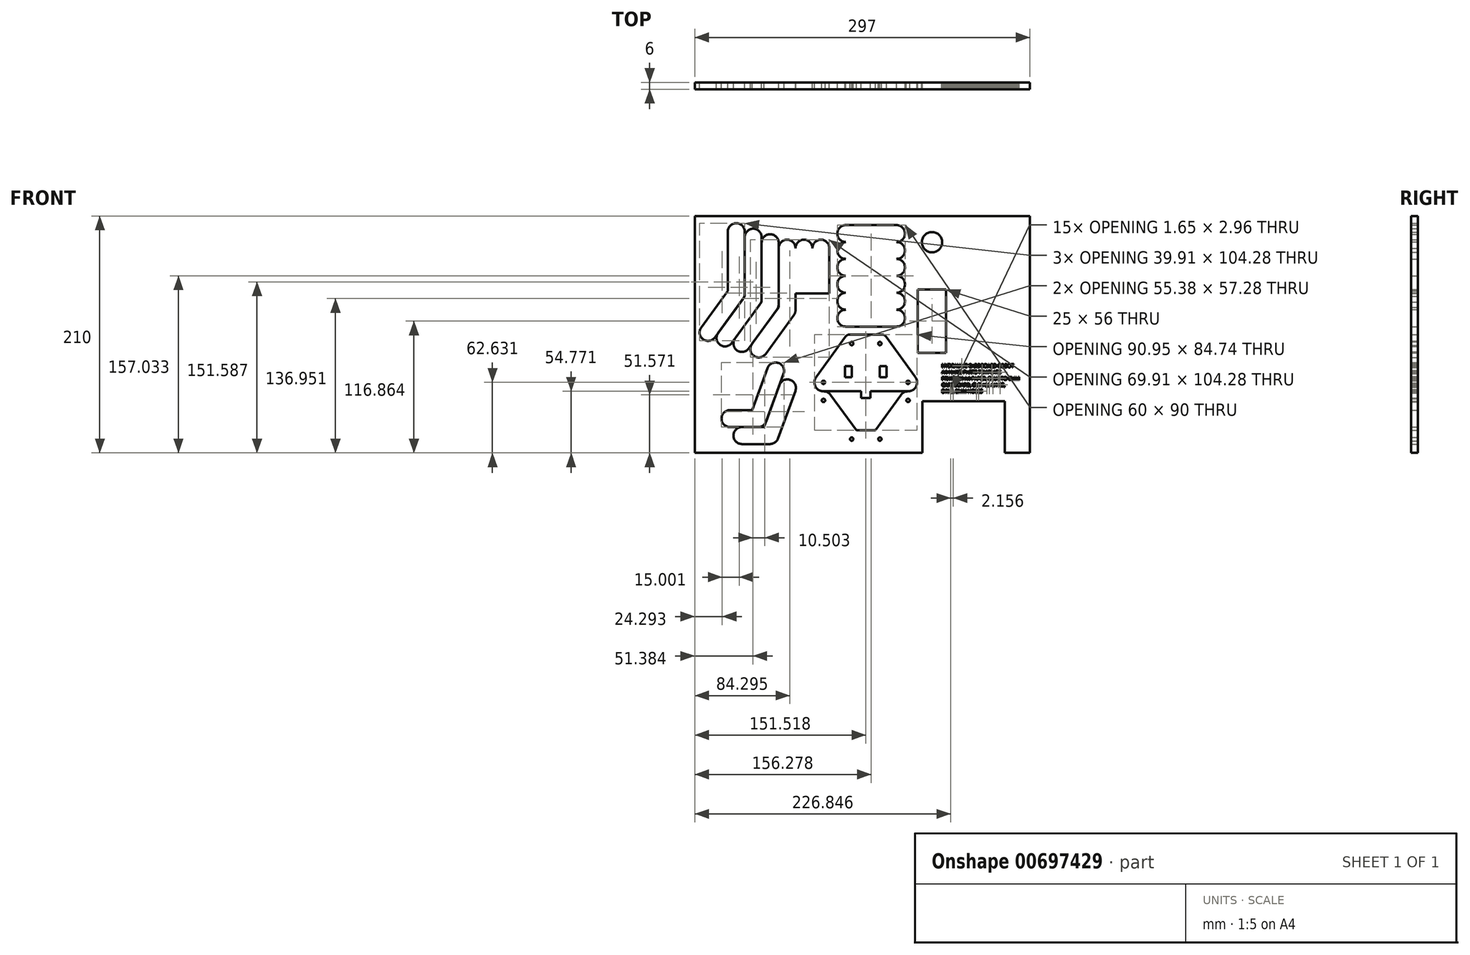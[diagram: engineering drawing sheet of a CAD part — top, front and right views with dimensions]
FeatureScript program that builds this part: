
annotation { "Feature Type Name" : "Feature", "Feature Type Description" : "" }
export const myFeature = defineFeature(function(context is Context, id is Id, definition is map)
    precondition{}
    {
        {
            var Q0;
            Q0=qCreatedBy(makeId("Front.planeOp"),FACE);
            var sketch = newSketch(context, id + "F0", { "sketchPlane" : qUnion([Q0])});
            skLineSegment(sketch, "E0.bottom", {"start": v(148.5, 105) * mm, "end": v(-148.5, 105) * mm});
            skLineSegment(sketch, "E0.top", {"start": v(148.5, -105) * mm, "end": v(-148.5, -105) * mm});
            skLineSegment(sketch, "E0.left", {"start": v(148.5, 105) * mm, "end": v(148.5, -105) * mm});
            skLineSegment(sketch, "E0.right", {"start": v(-148.5, 105) * mm, "end": v(-148.5, -105) * mm});
            skPoint(sketch, "E0.middle", {"position": v(0, 0) * mm});
            skLineSegment(sketch, "E1", {"start": v(-282.28, 34.37) * mm, "end": v(-269.78, 34.37) * mm, "construction": true});
            skLineSegment(sketch, "E2", {"start": v(-269.78, 34.37) * mm, "end": v(-269.78, 0) * mm, "construction": true});
            skLineSegment(sketch, "E3", {"start": v(-269.78, 0) * mm, "end": v(-307.28, 0) * mm, "construction": true});
            skLineSegment(sketch, "E4", {"start": v(-307.28, 0) * mm, "end": v(-282.28, 34.37) * mm, "construction": true});
            skLineSegment(sketch, "E5", {"start": v(-282.28, 34.37) * mm, "end": v(-297.67, 76.66) * mm, "construction": true});
            skLineSegment(sketch, "E6", {"start": v(-297.67, 76.66) * mm, "end": v(-322.67, 42.29) * mm, "construction": true});
            skLineSegment(sketch, "E7", {"start": v(-322.67, 42.29) * mm, "end": v(-307.28, 0) * mm, "construction": true});
            skLineSegment(sketch, "E8", {"start": v(-297.67, 76.66) * mm, "end": v(-297.67, 131.66) * mm, "construction": true});
            skLineSegment(sketch, "E9.MirrorCS", {"start": v(-216.89, 42.29) * mm, "end": v(-232.28, 0) * mm, "construction": true});
            skLineSegment(sketch, "E10.MirrorCS", {"start": v(-257.28, 34.37) * mm, "end": v(-241.89, 76.66) * mm, "construction": true});
            skArc(sketch, "E11.0.startCap", {"start": v(-290.17, 76.66) * mm, "mid": v(-297.67, 69.16) * mm, "end": v(-305.17, 76.66) * mm, "construction": true});
            skArc(sketch, "E11.0.endCap", {"start": v(-305.17, 131.66) * mm, "mid": v(-297.67, 139.16) * mm, "end": v(-290.17, 131.66) * mm, "construction": true});
            skLineSegment(sketch, "E11.0.left", {"start": v(-305.17, 76.66) * mm, "end": v(-305.17, 131.66) * mm, "construction": true});
            skLineSegment(sketch, "E11.0.right", {"start": v(-290.17, 76.66) * mm, "end": v(-290.17, 131.66) * mm, "construction": true});
            skArc(sketch, "E11.1.startCap", {"start": v(-303.74, 81.07) * mm, "mid": v(-293.26, 82.72) * mm, "end": v(-291.6, 72.24) * mm, "construction": true});
            skArc(sketch, "E11.1.endCap", {"start": v(-316.6, 37.87) * mm, "mid": v(-327.08, 36.22) * mm, "end": v(-328.74, 46.7) * mm, "construction": true});
            skLineSegment(sketch, "E11.1.left", {"start": v(-291.6, 72.24) * mm, "end": v(-316.6, 37.87) * mm, "construction": true});
            skLineSegment(sketch, "E11.1.right", {"start": v(-303.74, 81.07) * mm, "end": v(-328.74, 46.7) * mm, "construction": true});
            skArc(sketch, "E12.0.startCap", {"start": v(-250.23, 31.8) * mm, "mid": v(-259.85, 27.32) * mm, "end": v(-264.33, 36.93) * mm, "construction": true});
            skArc(sketch, "E12.0.endCap", {"start": v(-248.94, 79.22) * mm, "mid": v(-239.32, 83.7) * mm, "end": v(-234.84, 74.1) * mm, "construction": true});
            skLineSegment(sketch, "E12.0.left", {"start": v(-264.33, 36.93) * mm, "end": v(-248.94, 79.22) * mm, "construction": true});
            skLineSegment(sketch, "E12.0.right", {"start": v(-250.23, 31.8) * mm, "end": v(-234.84, 74.1) * mm, "construction": true});
            skLineSegment(sketch, "E13", {"start": v(-232.28, 0) * mm, "end": v(-257.28, 0) * mm, "construction": true});
            skArc(sketch, "E14.0.startCap", {"start": v(-232.28, 7.5) * mm, "mid": v(-224.78, 0) * mm, "end": v(-232.28, -7.5) * mm, "construction": true});
            skArc(sketch, "E14.0.endCap", {"start": v(-257.28, -7.5) * mm, "mid": v(-264.78, 0) * mm, "end": v(-257.28, 7.5) * mm, "construction": true});
            skLineSegment(sketch, "E14.0.left", {"start": v(-232.28, -7.5) * mm, "end": v(-257.28, -7.5) * mm, "construction": true});
            skLineSegment(sketch, "E14.0.right", {"start": v(-232.28, 7.5) * mm, "end": v(-257.28, 7.5) * mm, "construction": true});
            skArc(sketch, "E14.1.startCap", {"start": v(-223.94, 44.85) * mm, "mid": v(-214.32, 49.33) * mm, "end": v(-209.84, 39.72) * mm, "construction": true});
            skArc(sketch, "E14.1.endCap", {"start": v(-225.23, -2.57) * mm, "mid": v(-234.85, -7.05) * mm, "end": v(-239.33, 2.57) * mm, "construction": true});
            skLineSegment(sketch, "E14.1.left", {"start": v(-209.84, 39.72) * mm, "end": v(-225.23, -2.57) * mm, "construction": true});
            skLineSegment(sketch, "E14.1.right", {"start": v(-223.94, 44.85) * mm, "end": v(-239.33, 2.57) * mm, "construction": true});
            skLineSegment(sketch, "E15", {"start": v(-111.75, 36.23) * mm, "end": v(-111.75, 91.23) * mm, "construction": true});
            skLineSegment(sketch, "E16", {"start": v(-111.75, 36.23) * mm, "end": v(-136.75, 1.86) * mm, "construction": true});
            skArc(sketch, "E17.0.startCap", {"start": v(-104.25, 36.23) * mm, "mid": v(-104.62, 33.9) * mm, "end": v(-105.69, 31.81) * mm});
            skArc(sketch, "E17.0.endCap", {"start": v(-119.25, 91.23) * mm, "mid": v(-111.75, 98.73) * mm, "end": v(-104.25, 91.23) * mm});
            skLineSegment(sketch, "E17.0.left", {"start": v(-119.25, 38.66) * mm, "end": v(-119.25, 91.23) * mm});
            skLineSegment(sketch, "E17.0.right", {"start": v(-104.25, 36.23) * mm, "end": v(-104.25, 91.23) * mm});
            skArc(sketch, "E17.1.startCap", {"start": v(-104.25, 36.23) * mm, "mid": v(-104.62, 33.9) * mm, "end": v(-105.69, 31.81) * mm});
            skArc(sketch, "E17.1.endCap", {"start": v(-130.69, -2.56) * mm, "mid": v(-141.16, -4.2) * mm, "end": v(-142.82, 6.27) * mm});
            skLineSegment(sketch, "E17.1.left", {"start": v(-105.69, 31.81) * mm, "end": v(-130.69, -2.56) * mm});
            skLineSegment(sketch, "E17.1.right", {"start": v(-119.25, 38.66) * mm, "end": v(-142.82, 6.27) * mm});
            skCircle(sketch, "E18", {"center": v(-111.75, 91.23) * mm, "radius": 1.5 * mm});
            skCircle(sketch, "E19", {"center": v(-111.75, 36.23) * mm, "radius": 1.5 * mm});
            skCircle(sketch, "E20", {"center": v(-136.75, 1.86) * mm, "radius": 1.5 * mm});
            skLineSegment(sketch, "E21", {"start": v(-14.72, 89.53) * mm, "end": v(30.28, 89.53) * mm, "construction": true});
            skArc(sketch, "E22.0.startCap", {"start": v(-14.72, 82.03) * mm, "mid": v(-22.22, 89.53) * mm, "end": v(-14.72, 97.03) * mm});
            skArc(sketch, "E22.0.endCap", {"start": v(30.28, 97.03) * mm, "mid": v(37.78, 89.53) * mm, "end": v(30.28, 82.03) * mm});
            skLineSegment(sketch, "E22.0.left", {"start": v(-14.72, 97.03) * mm, "end": v(30.28, 97.03) * mm});
            skLineSegment(sketch, "E22.0.right", {"start": v(-14.72, 82.03) * mm, "end": v(30.28, 82.03) * mm});
            skCircle(sketch, "E23", {"center": v(-14.72, 89.53) * mm, "radius": 1.5 * mm});
            skCircle(sketch, "E24", {"center": v(30.28, 89.53) * mm, "radius": 1.5 * mm});
            skCircle(sketch, "E25.0.1.1", {"center": v(30.28, 74.53) * mm, "radius": 1.5 * mm});
            skCircle(sketch, "E25.0.1.2", {"center": v(-14.72, 74.53) * mm, "radius": 1.5 * mm});
            skArc(sketch, "E25.0.1.3", {"start": v(30.28, 82.03) * mm, "mid": v(37.78, 74.53) * mm, "end": v(30.28, 67.03) * mm});
            skArc(sketch, "E25.0.1.4", {"start": v(-14.72, 67.03) * mm, "mid": v(-22.22, 74.53) * mm, "end": v(-14.72, 82.03) * mm});
            skLineSegment(sketch, "E25.0.1.5", {"start": v(-14.72, 67.03) * mm, "end": v(30.28, 67.03) * mm});
            skLineSegment(sketch, "E25.0.1.6", {"start": v(-14.72, 74.53) * mm, "end": v(30.28, 74.53) * mm, "construction": true});
            skLineSegment(sketch, "E25.0.2.0", {"start": v(-14.72, 67.03) * mm, "end": v(30.28, 67.03) * mm});
            skCircle(sketch, "E25.0.2.1", {"center": v(30.28, 59.53) * mm, "radius": 1.5 * mm});
            skCircle(sketch, "E25.0.2.2", {"center": v(-14.72, 59.53) * mm, "radius": 1.5 * mm});
            skArc(sketch, "E25.0.2.3", {"start": v(30.28, 67.03) * mm, "mid": v(37.78, 59.53) * mm, "end": v(30.28, 52.03) * mm});
            skArc(sketch, "E25.0.2.4", {"start": v(-14.72, 52.03) * mm, "mid": v(-22.22, 59.53) * mm, "end": v(-14.72, 67.03) * mm});
            skLineSegment(sketch, "E25.0.2.5", {"start": v(-14.72, 52.03) * mm, "end": v(30.28, 52.03) * mm});
            skLineSegment(sketch, "E25.0.2.6", {"start": v(-14.72, 59.53) * mm, "end": v(30.28, 59.53) * mm, "construction": true});
            skLineSegment(sketch, "E25.0.3.0", {"start": v(-14.72, 52.03) * mm, "end": v(30.28, 52.03) * mm});
            skCircle(sketch, "E25.0.3.1", {"center": v(30.28, 44.53) * mm, "radius": 1.5 * mm});
            skCircle(sketch, "E25.0.3.2", {"center": v(-14.72, 44.53) * mm, "radius": 1.5 * mm});
            skArc(sketch, "E25.0.3.3", {"start": v(30.28, 52.03) * mm, "mid": v(37.78, 44.53) * mm, "end": v(30.28, 37.03) * mm});
            skArc(sketch, "E25.0.3.4", {"start": v(-14.72, 37.03) * mm, "mid": v(-22.22, 44.53) * mm, "end": v(-14.72, 52.03) * mm});
            skLineSegment(sketch, "E25.0.3.5", {"start": v(-14.72, 37.03) * mm, "end": v(30.28, 37.03) * mm});
            skLineSegment(sketch, "E25.0.3.6", {"start": v(-14.72, 44.53) * mm, "end": v(30.28, 44.53) * mm, "construction": true});
            skLineSegment(sketch, "E25.0.4.0", {"start": v(-14.72, 37.03) * mm, "end": v(30.28, 37.03) * mm});
            skCircle(sketch, "E25.0.4.1", {"center": v(30.28, 29.53) * mm, "radius": 1.5 * mm});
            skCircle(sketch, "E25.0.4.2", {"center": v(-14.72, 29.53) * mm, "radius": 1.5 * mm});
            skArc(sketch, "E25.0.4.3", {"start": v(30.28, 37.03) * mm, "mid": v(37.78, 29.53) * mm, "end": v(30.28, 22.03) * mm});
            skArc(sketch, "E25.0.4.4", {"start": v(-14.72, 22.03) * mm, "mid": v(-22.22, 29.53) * mm, "end": v(-14.72, 37.03) * mm});
            skLineSegment(sketch, "E25.0.4.5", {"start": v(-14.72, 22.03) * mm, "end": v(30.28, 22.03) * mm});
            skLineSegment(sketch, "E25.0.4.6", {"start": v(-14.72, 29.53) * mm, "end": v(30.28, 29.53) * mm, "construction": true});
            skLineSegment(sketch, "E25.0.5.0", {"start": v(-14.72, 22.03) * mm, "end": v(30.28, 22.03) * mm});
            skCircle(sketch, "E25.0.5.1", {"center": v(30.28, 14.53) * mm, "radius": 1.5 * mm});
            skCircle(sketch, "E25.0.5.2", {"center": v(-14.72, 14.53) * mm, "radius": 1.5 * mm});
            skArc(sketch, "E25.0.5.3", {"start": v(30.28, 22.03) * mm, "mid": v(37.78, 14.53) * mm, "end": v(30.28, 7.03) * mm});
            skArc(sketch, "E25.0.5.4", {"start": v(-14.72, 7.03) * mm, "mid": v(-22.22, 14.53) * mm, "end": v(-14.72, 22.03) * mm});
            skLineSegment(sketch, "E25.0.5.5", {"start": v(-14.72, 7.03) * mm, "end": v(30.28, 7.03) * mm});
            skLineSegment(sketch, "E25.0.5.6", {"start": v(-14.72, 14.53) * mm, "end": v(30.28, 14.53) * mm, "construction": true});
            skLineSegment(sketch, "E25.direction1", {"start": v(-14.72, 82.03) * mm, "end": v(10.98, 82.03) * mm, "construction": true});
            skLineSegment(sketch, "E25.direction2", {"start": v(-14.72, 82.03) * mm, "end": v(-14.72, 67.03) * mm, "construction": true});
            skLineSegment(sketch, "E26", {"start": v(-66.41, -47.28) * mm, "end": v(-81.8, -89.57) * mm, "construction": true});
            skLineSegment(sketch, "E27", {"start": v(-81.8, -89.57) * mm, "end": v(-106.8, -89.57) * mm, "construction": true});
            skArc(sketch, "E28.0.startCap", {"start": v(-73.46, -44.72) * mm, "mid": v(-63.85, -40.24) * mm, "end": v(-59.37, -49.85) * mm});
            skArc(sketch, "E28.0.endCap", {"start": v(-74.76, -92.13) * mm, "mid": v(-77.5, -95.71) * mm, "end": v(-81.8, -97.07) * mm});
            skLineSegment(sketch, "E28.0.left", {"start": v(-59.37, -49.85) * mm, "end": v(-74.76, -92.13) * mm});
            skLineSegment(sketch, "E28.0.right", {"start": v(-73.46, -44.72) * mm, "end": v(-87.06, -82.07) * mm});
            skArc(sketch, "E28.1.startCap", {"start": v(-74.76, -92.13) * mm, "mid": v(-77.5, -95.71) * mm, "end": v(-81.8, -97.07) * mm});
            skArc(sketch, "E28.1.endCap", {"start": v(-106.8, -97.07) * mm, "mid": v(-114.3, -89.57) * mm, "end": v(-106.8, -82.07) * mm});
            skLineSegment(sketch, "E28.1.left", {"start": v(-81.8, -97.07) * mm, "end": v(-106.8, -97.07) * mm});
            skLineSegment(sketch, "E28.1.right", {"start": v(-87.06, -82.07) * mm, "end": v(-106.8, -82.07) * mm});
            skCircle(sketch, "E29", {"center": v(-106.8, -89.57) * mm, "radius": 1.5 * mm});
            skCircle(sketch, "E30", {"center": v(-81.8, -89.57) * mm, "radius": 1.5 * mm});
            skCircle(sketch, "E31", {"center": v(-66.41, -47.28) * mm, "radius": 1.5 * mm});
            skArc(sketch, "E32.0.1.0", {"start": v(-83.96, -29.72) * mm, "mid": v(-74.35, -25.24) * mm, "end": v(-69.87, -34.85) * mm});
            skLineSegment(sketch, "E32.0.1.1", {"start": v(-76.92, -32.28) * mm, "end": v(-92.3, -74.57) * mm, "construction": true});
            skLineSegment(sketch, "E32.0.1.2", {"start": v(-97.56, -67.07) * mm, "end": v(-117.3, -67.07) * mm});
            skLineSegment(sketch, "E32.0.1.3", {"start": v(-69.87, -34.85) * mm, "end": v(-85.26, -77.13) * mm});
            skLineSegment(sketch, "E32.0.1.4", {"start": v(-92.3, -82.07) * mm, "end": v(-117.3, -82.07) * mm});
            skArc(sketch, "E32.0.1.5", {"start": v(-85.26, -77.13) * mm, "mid": v(-88, -80.71) * mm, "end": v(-92.3, -82.07) * mm});
            skCircle(sketch, "E32.0.1.6", {"center": v(-117.3, -74.57) * mm, "radius": 1.5 * mm});
            skCircle(sketch, "E32.0.1.7", {"center": v(-76.92, -32.28) * mm, "radius": 1.5 * mm});
            skArc(sketch, "E32.0.1.8", {"start": v(-117.3, -82.07) * mm, "mid": v(-124.8, -74.57) * mm, "end": v(-117.3, -67.07) * mm});
            skLineSegment(sketch, "E32.0.1.9", {"start": v(-92.3, -74.57) * mm, "end": v(-117.3, -74.57) * mm, "construction": true});
            skCircle(sketch, "E32.0.1.10", {"center": v(-92.3, -74.57) * mm, "radius": 1.5 * mm});
            skLineSegment(sketch, "E32.0.1.11", {"start": v(-83.96, -29.72) * mm, "end": v(-97.56, -67.07) * mm});
            skArc(sketch, "E32.0.1.12", {"start": v(-85.26, -77.13) * mm, "mid": v(-88, -80.71) * mm, "end": v(-92.3, -82.07) * mm});
            skLineSegment(sketch, "E32.direction1", {"start": v(-106.8, -97.07) * mm, "end": v(-72.94, -97.07) * mm, "construction": true});
            skLineSegment(sketch, "E32.direction2", {"start": v(-106.8, -97.07) * mm, "end": v(-117.3, -82.07) * mm, "construction": true});
            skLineSegment(sketch, "E33.1.0.0", {"start": v(-104.25, 33.79) * mm, "end": v(-104.25, 86.35) * mm});
            skLineSegment(sketch, "E33.1.0.1", {"start": v(-90.69, 26.94) * mm, "end": v(-115.69, -7.43) * mm});
            skLineSegment(sketch, "E33.1.0.2", {"start": v(-104.25, 33.79) * mm, "end": v(-127.82, 1.39) * mm});
            skCircle(sketch, "E33.1.0.3", {"center": v(-96.75, 31.35) * mm, "radius": 1.5 * mm});
            skArc(sketch, "E33.1.0.4", {"start": v(-89.25, 31.35) * mm, "mid": v(-89.62, 29.03) * mm, "end": v(-90.69, 26.94) * mm});
            skCircle(sketch, "E33.1.0.5", {"center": v(-121.75, -3.02) * mm, "radius": 1.5 * mm});
            skLineSegment(sketch, "E33.1.0.6", {"start": v(-96.75, 31.35) * mm, "end": v(-121.75, -3.02) * mm, "construction": true});
            skCircle(sketch, "E33.1.0.7", {"center": v(-96.75, 86.35) * mm, "radius": 1.5 * mm});
            skArc(sketch, "E33.1.0.8", {"start": v(-115.69, -7.43) * mm, "mid": v(-126.16, -9.09) * mm, "end": v(-127.82, 1.39) * mm});
            skArc(sketch, "E33.1.0.9", {"start": v(-89.25, 31.35) * mm, "mid": v(-89.62, 29.03) * mm, "end": v(-90.69, 26.94) * mm});
            skLineSegment(sketch, "E33.1.0.10", {"start": v(-96.75, 31.35) * mm, "end": v(-96.75, 86.35) * mm, "construction": true});
            skLineSegment(sketch, "E33.1.0.11", {"start": v(-89.25, 31.35) * mm, "end": v(-89.25, 86.35) * mm});
            skArc(sketch, "E33.1.0.12", {"start": v(-104.25, 86.35) * mm, "mid": v(-96.75, 93.85) * mm, "end": v(-89.25, 86.35) * mm});
            skLineSegment(sketch, "E33.2.0.0", {"start": v(-89.25, 28.9) * mm, "end": v(-89.25, 81.47) * mm});
            skLineSegment(sketch, "E33.2.0.1", {"start": v(-75.69, 22.06) * mm, "end": v(-100.69, -12.31) * mm});
            skLineSegment(sketch, "E33.2.0.2", {"start": v(-89.25, 28.9) * mm, "end": v(-112.82, -3.49) * mm});
            skCircle(sketch, "E33.2.0.3", {"center": v(-81.75, 26.47) * mm, "radius": 1.5 * mm});
            skArc(sketch, "E33.2.0.4", {"start": v(-74.25, 26.47) * mm, "mid": v(-74.62, 24.15) * mm, "end": v(-75.69, 22.06) * mm});
            skCircle(sketch, "E33.2.0.5", {"center": v(-106.75, -7.9) * mm, "radius": 1.5 * mm});
            skLineSegment(sketch, "E33.2.0.6", {"start": v(-81.75, 26.47) * mm, "end": v(-106.75, -7.9) * mm, "construction": true});
            skCircle(sketch, "E33.2.0.7", {"center": v(-81.75, 81.47) * mm, "radius": 1.5 * mm});
            skArc(sketch, "E33.2.0.8", {"start": v(-100.69, -12.31) * mm, "mid": v(-111.16, -13.97) * mm, "end": v(-112.82, -3.49) * mm});
            skArc(sketch, "E33.2.0.9", {"start": v(-74.25, 26.47) * mm, "mid": v(-74.62, 24.15) * mm, "end": v(-75.69, 22.06) * mm});
            skLineSegment(sketch, "E33.2.0.10", {"start": v(-81.75, 26.47) * mm, "end": v(-81.75, 81.47) * mm, "construction": true});
            skLineSegment(sketch, "E33.2.0.11", {"start": v(-74.25, 26.47) * mm, "end": v(-74.25, 81.47) * mm});
            skArc(sketch, "E33.2.0.12", {"start": v(-89.25, 81.47) * mm, "mid": v(-81.75, 88.97) * mm, "end": v(-74.25, 81.47) * mm});
            skLineSegment(sketch, "E33.3.0.0", {"start": v(-74.25, 24.03) * mm, "end": v(-74.25, 76.59) * mm});
            skLineSegment(sketch, "E33.3.0.1", {"start": v(-60.69, 17.18) * mm, "end": v(-85.69, -17.2) * mm});
            skLineSegment(sketch, "E33.3.0.2", {"start": v(-74.25, 24.03) * mm, "end": v(-97.82, -8.37) * mm});
            skCircle(sketch, "E33.3.0.3", {"center": v(-66.75, 21.59) * mm, "radius": 1.5 * mm});
            skArc(sketch, "E33.3.0.4", {"start": v(-59.25, 21.59) * mm, "mid": v(-59.62, 19.27) * mm, "end": v(-60.69, 17.18) * mm});
            skCircle(sketch, "E33.3.0.5", {"center": v(-91.75, -12.78) * mm, "radius": 1.5 * mm});
            skLineSegment(sketch, "E33.3.0.6", {"start": v(-66.75, 21.59) * mm, "end": v(-91.75, -12.78) * mm, "construction": true});
            skCircle(sketch, "E33.3.0.7", {"center": v(-66.75, 76.59) * mm, "radius": 1.5 * mm});
            skArc(sketch, "E33.3.0.8", {"start": v(-85.69, -17.2) * mm, "mid": v(-96.16, -18.84) * mm, "end": v(-97.82, -8.37) * mm});
            skArc(sketch, "E33.3.0.9", {"start": v(-59.25, 21.59) * mm, "mid": v(-59.62, 19.27) * mm, "end": v(-60.69, 17.18) * mm});
            skLineSegment(sketch, "E33.3.0.10", {"start": v(-66.75, 21.59) * mm, "end": v(-66.75, 76.59) * mm, "construction": true});
            skLineSegment(sketch, "E33.3.0.11", {"start": v(-59.25, 21.59) * mm, "end": v(-59.25, 76.59) * mm});
            skArc(sketch, "E33.3.0.12", {"start": v(-74.25, 76.59) * mm, "mid": v(-66.75, 84.09) * mm, "end": v(-59.25, 76.59) * mm});
            skLineSegment(sketch, "E33.direction1", {"start": v(-142.82, 6.27) * mm, "end": v(-127.82, 1.39) * mm, "construction": true});
            skLineSegment(sketch, "E34", {"start": v(3.02, -8) * mm, "end": v(-9.48, -8) * mm, "construction": true});
            skLineSegment(sketch, "E35", {"start": v(-9.48, -8) * mm, "end": v(-34.48, -42.37) * mm, "construction": true});
            skLineSegment(sketch, "E36", {"start": v(-34.48, -42.37) * mm, "end": v(3.02, -42.37) * mm, "construction": true});
            skLineSegment(sketch, "E37", {"start": v(3.02, -42.37) * mm, "end": v(3.02, -8) * mm, "construction": true});
            skLineSegment(sketch, "E38.0", {"start": v(3.02, 0) * mm, "end": v(-11, 0) * mm});
            skLineSegment(sketch, "E38.2", {"start": v(-34.48, -50.37) * mm, "end": v(-0.98, -50.37) * mm});
            skLineSegment(sketch, "E38.3", {"start": v(-15.05, -2.06) * mm, "end": v(-40.95, -37.66) * mm});
            skPoint(sketch, "E39.visualSharp", {"position": v(-13.56, 0) * mm});
            skArc(sketch, "E39.filletArc", {"start": v(-11, 0) * mm, "mid": v(-13.28, -0.54) * mm, "end": v(-15.05, -2.06) * mm});
            skPoint(sketch, "E40.visualSharp", {"position": v(-50.2, -50.37) * mm});
            skLineSegment(sketch, "E41", {"start": v(3.02, -8) * mm, "end": v(3.02, 0) * mm, "construction": true});
            skLineSegment(sketch, "E42", {"start": v(3.02, -42.37) * mm, "end": v(3.02, -50.37) * mm, "construction": true});
            skCircle(sketch, "E43", {"center": v(-9.48, -8) * mm, "radius": 1.5 * mm});
            skCircle(sketch, "E44", {"center": v(-34.48, -42.37) * mm, "radius": 1.5 * mm});
            skLineSegment(sketch, "E45.MirrorCS", {"start": v(40.52, -50.37) * mm, "end": v(7.02, -50.37) * mm});
            skArc(sketch, "E46.MirrorCS", {"start": v(17.05, 0) * mm, "mid": v(19.31, -0.54) * mm, "end": v(21.09, -2.06) * mm});
            skLineSegment(sketch, "E47.MirrorCS", {"start": v(40.52, -42.37) * mm, "end": v(3.02, -42.37) * mm, "construction": true});
            skCircle(sketch, "E48.MirrorC", {"center": v(15.52, -8) * mm, "radius": 1.5 * mm});
            skLineSegment(sketch, "E49.MirrorCS", {"start": v(21.09, -2.06) * mm, "end": v(46.99, -37.66) * mm});
            skLineSegment(sketch, "E50.MirrorCS", {"start": v(3.02, -8) * mm, "end": v(15.52, -8) * mm, "construction": true});
            skCircle(sketch, "E51.MirrorC", {"center": v(40.52, -42.37) * mm, "radius": 1.5 * mm});
            skPoint(sketch, "E52.MirrorP", {"position": v(19.6, 0) * mm});
            skLineSegment(sketch, "E53.MirrorCS", {"start": v(15.52, -8) * mm, "end": v(40.52, -42.37) * mm, "construction": true});
            skLineSegment(sketch, "E54.MirrorCS", {"start": v(3.02, 0) * mm, "end": v(17.05, 0) * mm});
            skLineSegment(sketch, "E55.MirrorCS", {"start": v(3.02, -58.37) * mm, "end": v(3.02, -50.37) * mm, "construction": true});
            skLineSegment(sketch, "E56.MirrorCS", {"start": v(3.02, -100.74) * mm, "end": v(17.05, -100.74) * mm});
            skPoint(sketch, "E57.MirrorP", {"position": v(-13.56, -100.74) * mm});
            skLineSegment(sketch, "E58.MirrorCS", {"start": v(3.02, -92.74) * mm, "end": v(15.52, -92.74) * mm, "construction": true});
            skLineSegment(sketch, "E59.MirrorCS", {"start": v(40.52, -58.37) * mm, "end": v(3.02, -58.37) * mm, "construction": true});
            skLineSegment(sketch, "E60.MirrorCS", {"start": v(3.02, -100.74) * mm, "end": v(-11, -100.74) * mm});
            skLineSegment(sketch, "E61.MirrorCS", {"start": v(3.02, -92.74) * mm, "end": v(-9.48, -92.74) * mm, "construction": true});
            skCircle(sketch, "E62.MirrorC", {"center": v(-9.48, -92.74) * mm, "radius": 1.5 * mm});
            skArc(sketch, "E63.MirrorCS", {"start": v(-11, -100.74) * mm, "mid": v(-13.28, -100.2) * mm, "end": v(-15.05, -98.68) * mm});
            skLineSegment(sketch, "E64.MirrorCS", {"start": v(-9.48, -92.74) * mm, "end": v(-34.48, -58.37) * mm, "construction": true});
            skCircle(sketch, "E65.MirrorC", {"center": v(-34.48, -58.37) * mm, "radius": 1.5 * mm});
            skCircle(sketch, "E66.MirrorC", {"center": v(40.52, -58.37) * mm, "radius": 1.5 * mm});
            skCircle(sketch, "E67.MirrorC", {"center": v(15.52, -92.74) * mm, "radius": 1.5 * mm});
            skLineSegment(sketch, "E68.MirrorCS", {"start": v(-15.05, -98.68) * mm, "end": v(-40.95, -63.08) * mm});
            skPoint(sketch, "E69.MirrorP", {"position": v(19.6, -100.74) * mm});
            skLineSegment(sketch, "E70.MirrorCS", {"start": v(-34.48, -58.37) * mm, "end": v(3.02, -58.37) * mm, "construction": true});
            skLineSegment(sketch, "E71.MirrorCS", {"start": v(3.02, -92.74) * mm, "end": v(3.02, -100.74) * mm, "construction": true});
            skLineSegment(sketch, "E72.MirrorCS", {"start": v(15.52, -92.74) * mm, "end": v(40.52, -58.37) * mm, "construction": true});
            skLineSegment(sketch, "E73.MirrorCS", {"start": v(21.09, -98.68) * mm, "end": v(46.99, -63.08) * mm});
            skArc(sketch, "E74.MirrorCS", {"start": v(17.05, -100.74) * mm, "mid": v(19.31, -100.2) * mm, "end": v(21.09, -98.68) * mm});
            skLineSegment(sketch, "E75.MirrorCS", {"start": v(3.02, -58.37) * mm, "end": v(3.02, -92.74) * mm, "construction": true});
            skLineSegment(sketch, "E76.bottom", {"start": v(-15.48, -27.87) * mm, "end": v(-9.48, -27.87) * mm});
            skLineSegment(sketch, "E76.top", {"start": v(-15.48, -37.87) * mm, "end": v(-9.48, -37.87) * mm});
            skLineSegment(sketch, "E76.left", {"start": v(-15.48, -27.87) * mm, "end": v(-15.48, -37.87) * mm});
            skLineSegment(sketch, "E76.right", {"start": v(-9.48, -27.87) * mm, "end": v(-9.48, -37.87) * mm});
            skLineSegment(sketch, "E77.MirrorCS", {"start": v(21.52, -27.87) * mm, "end": v(21.52, -37.87) * mm});
            skLineSegment(sketch, "E78.MirrorCS", {"start": v(21.52, -37.87) * mm, "end": v(15.52, -37.87) * mm});
            skLineSegment(sketch, "E79.MirrorCS", {"start": v(21.52, -27.87) * mm, "end": v(15.52, -27.87) * mm});
            skLineSegment(sketch, "E80.MirrorCS", {"start": v(15.52, -27.87) * mm, "end": v(15.52, -37.87) * mm});
            skLineSegment(sketch, "E81", {"start": v(7.02, -50.37) * mm, "end": v(7.02, -56.37) * mm});
            skLineSegment(sketch, "E82", {"start": v(7.02, -56.37) * mm, "end": v(-0.98, -56.37) * mm});
            skLineSegment(sketch, "E83", {"start": v(-0.98, -56.37) * mm, "end": v(-0.98, -50.37) * mm});
            skPoint(sketch, "E84.orphan", {"position": v(3.02, -50.37) * mm});
            skPoint(sketch, "E85", {"position": v(3.02, -56.37) * mm});
            skLineSegment(sketch, "E86.bottom", {"start": v(49.18, 95.86) * mm, "end": v(74.18, 95.86) * mm});
            skLineSegment(sketch, "E86.top", {"start": v(49.18, 39.86) * mm, "end": v(74.18, 39.86) * mm});
            skLineSegment(sketch, "E86.left", {"start": v(49.18, 95.86) * mm, "end": v(49.18, 39.86) * mm});
            skLineSegment(sketch, "E86.right", {"start": v(74.18, 95.86) * mm, "end": v(74.18, 39.86) * mm});
            skCircle(sketch, "E87", {"center": v(61.68, 81.86) * mm, "radius": 9 * mm});
            skPoint(sketch, "E87.centerSnap0", {"position": v(61.68, 95.86) * mm});
            skLineSegment(sketch, "E88.MirrorCS", {"start": v(49.18, -16.14) * mm, "end": v(74.18, -16.14) * mm});
            skLineSegment(sketch, "E89.MirrorCS", {"start": v(49.18, -16.14) * mm, "end": v(49.18, 39.86) * mm});
            skCircle(sketch, "E90.MirrorC", {"center": v(61.68, -2.14) * mm, "radius": 9 * mm});
            skPoint(sketch, "E91.MirrorP", {"position": v(61.68, -16.14) * mm});
            skLineSegment(sketch, "E92.MirrorCS", {"start": v(74.18, -16.14) * mm, "end": v(74.18, 39.86) * mm});
            skCircle(sketch, "E93", {"center": v(-66.75, 21.59) * mm, "radius": 7.5 * mm, "construction": true});
            skLineSegment(sketch, "E94", {"start": v(-74.25, 36.59) * mm, "end": v(-59.25, 36.59) * mm, "construction": true});
            skLineSegment(sketch, "E95.1.0.0", {"start": v(-51.75, 21.59) * mm, "end": v(-51.75, 76.59) * mm, "construction": true});
            skArc(sketch, "E95.1.0.2", {"start": v(-59.25, 76.59) * mm, "mid": v(-51.75, 84.09) * mm, "end": v(-44.25, 76.59) * mm});
            skLineSegment(sketch, "E95.1.0.3", {"start": v(-44.25, 21.59) * mm, "end": v(-44.25, 27.85) * mm, "construction": true});
            skCircle(sketch, "E95.1.0.4", {"center": v(-51.75, 76.59) * mm, "radius": 1.5 * mm});
            skLineSegment(sketch, "E95.direction1", {"start": v(-74.25, 76.59) * mm, "end": v(-59.25, 76.59) * mm, "construction": true});
            skLineSegment(sketch, "E96", {"start": v(-44.25, 27.85) * mm, "end": v(-44.25, 76.59) * mm});
            skLineSegment(sketch, "E97.0.2.0", {"start": v(-36.75, 21.59) * mm, "end": v(-36.75, 76.59) * mm, "construction": true});
            skArc(sketch, "E97.6.2.0", {"start": v(-44.25, 76.59) * mm, "mid": v(-36.75, 84.09) * mm, "end": v(-29.25, 76.59) * mm});
            skLineSegment(sketch, "E97.10.2.0", {"start": v(-29.25, 21.59) * mm, "end": v(-29.25, 36.59) * mm, "construction": true});
            skCircle(sketch, "E97.13.2.0", {"center": v(-36.75, 76.59) * mm, "radius": 1.5 * mm});
            skLineSegment(sketch, "E98", {"start": v(-29.25, 36.59) * mm, "end": v(-29.25, 76.59) * mm});
            skLineSegment(sketch, "E99", {"start": v(-29.25, 36.59) * mm, "end": v(-59.25, 36.59) * mm});
            skLineSegment(sketch, "E100", {"start": v(-119.25, 38.66) * mm, "end": v(-111.75, 36.23) * mm, "construction": true});
            skLineSegment(sketch, "E101", {"start": v(-119.25, 38.66) * mm, "end": v(-110.67, 50.47) * mm, "construction": true});
            skLineSegment(sketch, "E102", {"start": v(-92.3, -74.57) * mm, "end": v(-97.56, -67.07) * mm, "construction": true});
            skLineSegment(sketch, "E103", {"start": v(-92.3, -74.57) * mm, "end": v(-83.97, -74.57) * mm, "construction": true});
            skCircle(sketch, "E104", {"center": v(-260.8, -49.84) * mm, "radius": 25 * mm, "construction": true});
            skLineSegment(sketch, "E105", {"start": v(-260.8, -49.84) * mm, "end": v(-237.32, -58.39) * mm, "construction": true});
            skLineSegment(sketch, "E106", {"start": v(-252.26, -26.35) * mm, "end": v(-260.8, -49.84) * mm, "construction": true});
            skPoint(sketch, "E107.newPointA", {"position": v(-40.73, -50.37) * mm});
            skPoint(sketch, "E107.newPointB", {"position": v(-44.63, -42.71) * mm});
            skArc(sketch, "E107.filletArc", {"start": v(-40.95, -37.66) * mm, "mid": v(-41.57, -46.08) * mm, "end": v(-34.3, -50.37) * mm});
            skPoint(sketch, "E108.newPointA", {"position": v(50.66, -42.71) * mm});
            skPoint(sketch, "E108.newPointB", {"position": v(46.76, -50.37) * mm});
            skArc(sketch, "E108.filletArc", {"start": v(40.52, -50.37) * mm, "mid": v(47.65, -46) * mm, "end": v(46.99, -37.66) * mm});
            skPoint(sketch, "E109.newPointA", {"position": v(-44.63, -58.02) * mm});
            skArc(sketch, "E109.filletArc", {"start": v(-34.48, -50.37) * mm, "mid": v(-41.61, -54.74) * mm, "end": v(-40.95, -63.08) * mm});
            skPoint(sketch, "E110.newPointA", {"position": v(50.66, -58.02) * mm});
            skArc(sketch, "E110.filletArc", {"start": v(46.99, -63.08) * mm, "mid": v(47.65, -54.74) * mm, "end": v(40.52, -50.37) * mm});
            skLineSegment(sketch, "E111.0", {"start": v(-5.4, -84.74) * mm, "end": v(-28.01, -53.66) * mm});
            skLineSegment(sketch, "E111.1", {"start": v(3.02, -84.74) * mm, "end": v(-5.4, -84.74) * mm});
            skLineSegment(sketch, "E111.2", {"start": v(3.02, -84.74) * mm, "end": v(11.44, -84.74) * mm});
            skLineSegment(sketch, "E111.3", {"start": v(11.44, -84.74) * mm, "end": v(34.05, -53.66) * mm});
            skArc(sketch, "E112", {"start": v(-28.01, -53.66) * mm, "mid": v(-30.85, -51.24) * mm, "end": v(-34.48, -50.37) * mm});
            skArc(sketch, "E113", {"start": v(34.05, -53.66) * mm, "mid": v(36.89, -51.24) * mm, "end": v(40.52, -50.37) * mm});
            skLineSegment(sketch, "E114", {"start": v(-260.8, -49.84) * mm, "end": v(-223.3, -49.84) * mm, "construction": true});
            skLineSegment(sketch, "E115", {"start": v(-223.3, -49.84) * mm, "end": v(-223.3, -79.84) * mm, "construction": true});
            skLineSegment(sketch, "E116", {"start": v(-223.3, -79.84) * mm, "end": v(-223.3, -117.58) * mm, "construction": true});
            skLineSegment(sketch, "E117", {"start": v(-223.3, -117.58) * mm, "end": v(-237.32, -58.39) * mm, "construction": true});
            skLineSegment(sketch, "E118", {"start": v(-223.3, -79.84) * mm, "end": v(-252.26, -26.35) * mm, "construction": true});
            skPoint(sketch, "E119.endSnap0", {"position": v(-242.06, -49.84) * mm});
            skLineSegment(sketch, "E120", {"start": v(-215.41, -79.84) * mm, "end": v(-215.41, -204.84) * mm, "construction": true});
            skText(sketch, "E121", { "text": "HYDRAULIC CARDBOARD ROBOT\nA4 HAND PARTS TEMPLATE\nPRINT ON A4 PAPER, GLUE TO 6MM\nCARDBOARD, CUT ALL LINES,\nDRILL 2MM HOLES", "fontName": "OpenSans-Regular.ttf"});
            skLineSegment(sketch, "E122", {"start": v(59.48, -102.47) * mm, "end": v(59.48, -82.47) * mm});
            skLineSegment(sketch, "E123", {"start": v(59.48, -82.47) * mm, "end": v(120.3, -82.47) * mm});
            skLineSegment(sketch, "E124", {"start": v(120.3, -82.47) * mm, "end": v(120.3, -62.47) * mm});
            skArc(sketch, "E125.0.startCap", {"start": v(121.3, -82.47) * mm, "mid": v(120.3, -83.47) * mm, "end": v(119.3, -82.47) * mm});
            skArc(sketch, "E125.0.endCap", {"start": v(119.3, -62.47) * mm, "mid": v(120.3, -61.47) * mm, "end": v(121.3, -62.47) * mm});
            skLineSegment(sketch, "E125.0.left", {"start": v(119.3, -82.47) * mm, "end": v(119.3, -62.47) * mm});
            skLineSegment(sketch, "E125.0.right", {"start": v(121.3, -82.47) * mm, "end": v(121.3, -62.47) * mm});
            skArc(sketch, "E125.1.startCap", {"start": v(60.48, -102.47) * mm, "mid": v(59.48, -103.47) * mm, "end": v(58.48, -102.47) * mm});
            skArc(sketch, "E125.1.endCap", {"start": v(58.48, -82.47) * mm, "mid": v(59.48, -81.47) * mm, "end": v(60.48, -82.47) * mm});
            skLineSegment(sketch, "E125.1.left", {"start": v(58.48, -102.47) * mm, "end": v(58.48, -82.47) * mm});
            skLineSegment(sketch, "E125.1.right", {"start": v(60.48, -102.47) * mm, "end": v(60.48, -82.47) * mm});
            skArc(sketch, "E125.2.startCap", {"start": v(59.48, -83.47) * mm, "mid": v(58.48, -82.47) * mm, "end": v(59.48, -81.47) * mm});
            skArc(sketch, "E125.2.endCap", {"start": v(120.3, -81.47) * mm, "mid": v(121.3, -82.47) * mm, "end": v(120.3, -83.47) * mm});
            skLineSegment(sketch, "E125.2.left", {"start": v(59.48, -81.47) * mm, "end": v(120.3, -81.47) * mm});
            skLineSegment(sketch, "E125.2.right", {"start": v(59.48, -83.47) * mm, "end": v(120.3, -83.47) * mm});
            skText(sketch, "E126", { "text": "81mm push rod bending jig", "fontName": "OpenSans-Regular.ttf"});
            skLineSegment(sketch, "E127.bottom", {"start": v(53.16, -105) * mm, "end": v(126.3, -105) * mm});
            skLineSegment(sketch, "E127.top", {"start": v(53.16, -59.04) * mm, "end": v(126.3, -59.04) * mm});
            skLineSegment(sketch, "E127.left", {"start": v(53.16, -105) * mm, "end": v(53.16, -59.04) * mm});
            skLineSegment(sketch, "E127.right", {"start": v(126.3, -105) * mm, "end": v(126.3, -59.04) * mm});
            const initialGuessF0  = {"E121": [0.07036, -0.02912, 1, 0, 0.00299], "E126": [0.0588, -0.0725, 1, 0, 0.002]};
            skSetInitialGuess(sketch, initialGuessF0);
            skSolve(sketch);
        }
        {
            var Q0;
            {var subQ4=sQuery(id+"F0.wireOp",EDGE,"E17.0.endCap");Q0=makeQuery(id+"F0.imprint","IMPRINT",FACE,{"disambiguationData":[TD([[makeQuery(id+"F0.imprint","IMPRINT",EDGE,{"derivedFrom":subQ4}),-1.0]])]});}
            var Q1;
            {var subQ1=sQuery(id+"F0.wireOp",EDGE,"E95.1.0.2");Q1=makeQuery(id+"F0.imprint","IMPRINT",FACE,{"disambiguationData":[TD([[makeQuery(id+"F0.imprint","IMPRINT",EDGE,{"derivedFrom":subQ1}),-1.0]])]});}
            var Q2;
            Q2=makeQuery(id+"F0.imprint","IMPRINT",FACE,{"disambiguationData":[TD([[makeQuery(id+"F0.imprint","IMPRINT",EDGE,{"derivedFrom":sQuery(id+"F0.wireOp",EDGE,"E22.0.startCap")}),-1.0]])]});
            var Q3;
            Q3=makeQuery(id+"F0.imprint","IMPRINT",FACE,{"disambiguationData":[TD([[makeQuery(id+"F0.imprint","IMPRINT",EDGE,{"derivedFrom":sQuery(id+"F0.wireOp",EDGE,"E32.0.1.0")}),-1.0]])]});
            var Q4;
            Q4=makeQuery(id+"F0.imprint","IMPRINT",FACE,{"disambiguationData":[TD([[makeQuery(id+"F0.imprint","IMPRINT",EDGE,{"derivedFrom":sQuery(id+"F0.wireOp",EDGE,"E86.bottom")}),-1.0]])]});
            var Q5;
            Q5=makeQuery(id+"F0.imprint","IMPRINT",FACE,{"disambiguationData":[TD([[makeQuery(id+"F0.imprint","IMPRINT",EDGE,{"derivedFrom":sQuery(id+"F0.wireOp",EDGE,"E56.MirrorCS")}),1.0]])]});
            extrude(context, id + "F1", {"entities" : qUnion([Q0, Q1, Q2, Q3, Q4, Q5]), "depth" : 6 * mm, "offsetDistance" : 25 * mm});
        }
        {
            var Q0;
            Q0=makeQuery(id+"F0.imprint","IMPRINT",FACE,{"disambiguationData":[TD([[makeQuery(id+"F0.imprint","IMPRINT",EDGE,{"derivedFrom":sQuery(id+"F0.wireOp",EDGE,"E38.0")}),1.0]])]});
            extrude(context, id + "F2", {"entities" : qUnion([Q0]), "depth" : 6 * mm, "offsetDistance" : 25 * mm});
        }
    });
